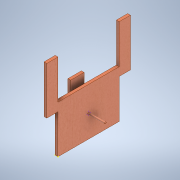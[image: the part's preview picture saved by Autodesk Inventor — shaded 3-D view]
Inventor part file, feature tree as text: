
AUTODESK INVENTOR PART (.ipt)
format: ipt  version: 2021 (Build 250183000, 183)  size: 198,656 bytes
history: native  units: mm
features: sketch x8, extrude x4
ambient origin geometry x8: Origin, YZ Plane, XZ Plane, XY Plane, X Axis, Y Axis, Z Axis, Center Point
bodies: Solid1 (feature_tree)
feature tree (12):
  extrude  "Extrusion1"  TaperAngle=90.0deg  [1 undecoded]
  sketch  "Sketch2"  dims[d2=70.0mm d3=0.0mm]
  extrude  "Extrusion2"  TaperAngle=0.0deg  [1 undecoded]
  sketch  "Sketch4"  dims[d6=0.0mm d7=20.0mm]
  sketch  "Sketch5"  dims[d8=70.0mm]
  sketch  "Sketch6"  dims[d9=110.0mm]
  extrude  "Extrusion3"  Depth=85.0mm
  extrude  "Extrusion4"  Depth=20.0mm
  sketch  "Sketch9"  dims[d11=70.0mm d12=90.0deg d13=20.0mm d14=90.0deg d15=85.0mm d16=90.0deg d17=5.0mm d18=0.0mm d19=3.0mm d20=30.0mm d21=0.0mm d22=24.0mm d23=5.0mm d24=20.0mm d25=0.0mm d26=5.0mm d27=45.0mm d28=0.0mm d39=0.5mm d40=0.872665mm d41=0.5mm d42=0.872665mm d43=0.872665mm]
  sketch  "Sketch1"  dims[d0=110.0mm d1=90.0deg]
  sketch  "Sketch3"  dims[d4=20.0mm d5=85.0mm]
  sketch  "Sketch7"  dims[d10=90.0deg]
note: 2 required parameter values undecoded (feature->parameter linkage not recoverable at this tier; creation-order binding heuristic only, values carry confidence <= 0.55)
